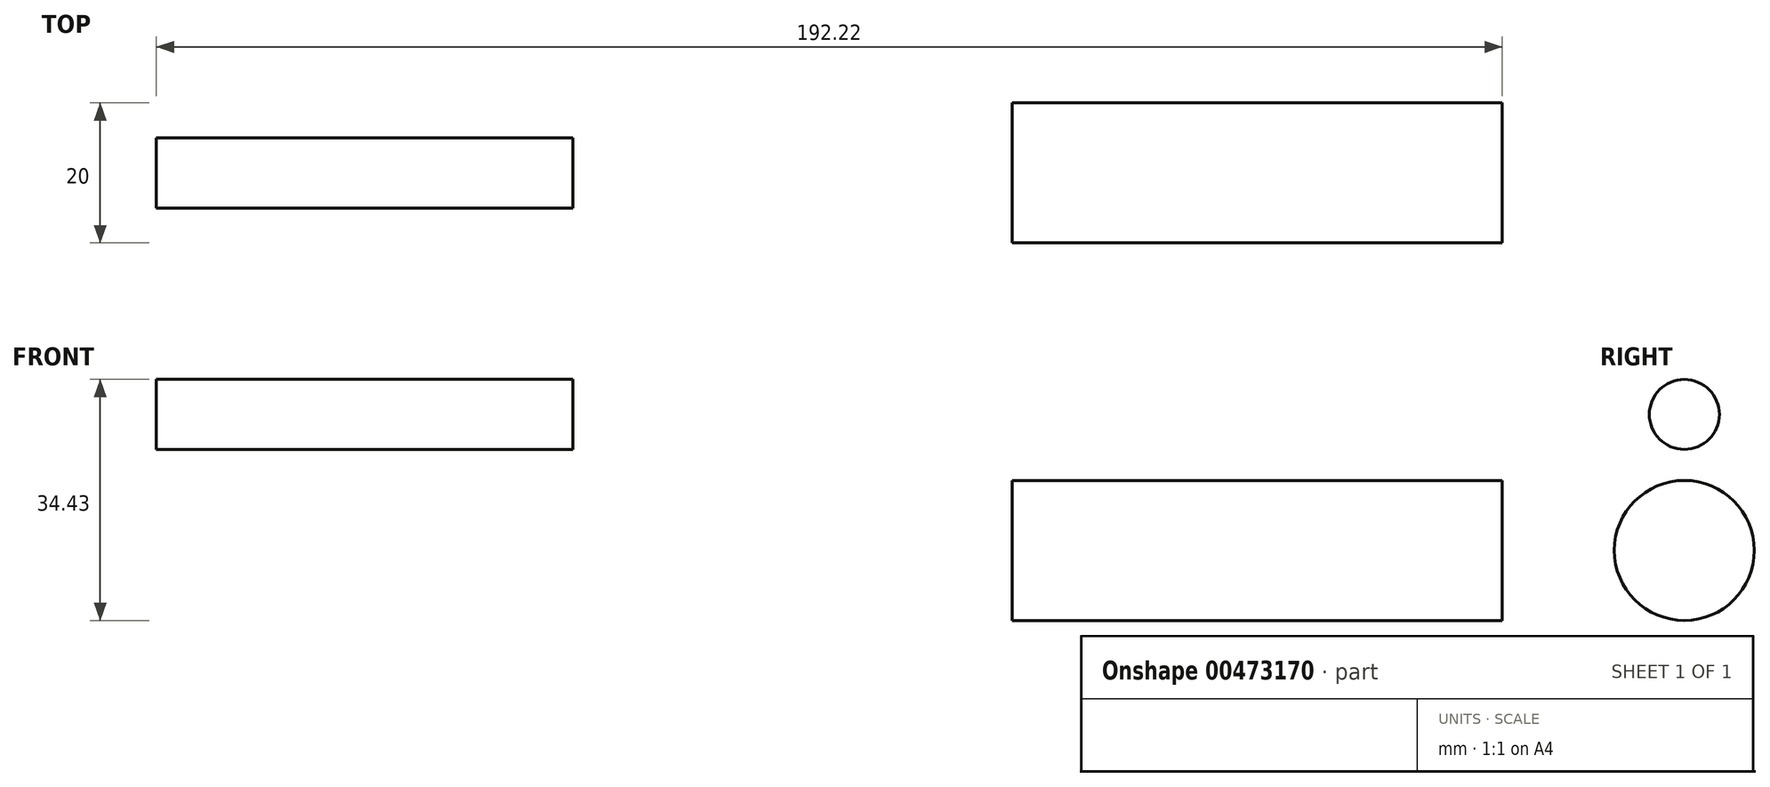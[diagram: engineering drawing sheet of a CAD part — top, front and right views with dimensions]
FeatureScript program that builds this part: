
annotation { "Feature Type Name" : "Feature", "Feature Type Description" : "" }
export const myFeature = defineFeature(function(context is Context, id is Id, definition is map)
    precondition{}
    {
        {
            var Q0;
            Q0=qCreatedBy(makeId("Front.planeOp"),FACE);
            var sketch = newSketch(context, id + "F0", { "sketchPlane" : qUnion([Q0])});
            skLineSegment(sketch, "E0.bottom", {"start": v(-86.95, 36.87) * mm, "end": v(-27.44, 36.87) * mm});
            skLineSegment(sketch, "E0.top", {"start": v(-86.95, 31.87) * mm, "end": v(-27.44, 31.87) * mm});
            skLineSegment(sketch, "E0.left", {"start": v(-86.95, 36.87) * mm, "end": v(-86.95, 31.87) * mm});
            skLineSegment(sketch, "E0.right", {"start": v(-27.44, 36.87) * mm, "end": v(-27.44, 31.87) * mm});
            skLineSegment(sketch, "E1", {"start": v(-32.57, 31.87) * mm, "end": v(-94.5, 31.87) * mm, "construction": true});
            skSolve(sketch);
        }
        {
            var Q0;
            Q0=makeQuery(id+"F0.imprint","IMPRINT",FACE,{"disambiguationData":[TD([[makeQuery(id+"F0.imprint","IMPRINT",EDGE,{"derivedFrom":sQuery(id+"F0.wireOp",EDGE,"E0.bottom")}),-1.0]])]});
            var Q1;
            Q1=sQuery(id+"F0.wireOp",EDGE,"E1");
            revolve(context, id + "F1", {"surfaceOperationType" : NewSurfaceOperationType.NEW, "entities" : qUnion([Q0]), "axis" : qUnion([Q1]), "revolveType" : RevolveType.FULL});
        }
        {
            var Q0;
            Q0=qCreatedBy(makeId("Front.planeOp"),FACE);
            var sketch = newSketch(context, id + "F2", { "sketchPlane" : qUnion([Q0])});
            skLineSegment(sketch, "E2.bottom", {"start": v(35.27, 22.44) * mm, "end": v(105.27, 22.44) * mm});
            skLineSegment(sketch, "E2.top", {"start": v(35.27, 12.44) * mm, "end": v(105.27, 12.44) * mm});
            skLineSegment(sketch, "E2.left", {"start": v(35.27, 22.44) * mm, "end": v(35.27, 12.44) * mm});
            skLineSegment(sketch, "E2.right", {"start": v(105.27, 22.44) * mm, "end": v(105.27, 12.44) * mm});
            skSolve(sketch);
        }
        {
            var Q0;
            Q0 = qSketchRegion(id + "F2", true);
            var Q1;
            Q1=sQuery(id+"F2.wireOp",EDGE,"E2.top");
            revolve(context, id + "F3", {"surfaceOperationType" : NewSurfaceOperationType.NEW, "entities" : qUnion([Q0]), "axis" : qUnion([Q1]), "revolveType" : RevolveType.FULL});
        }
    });
